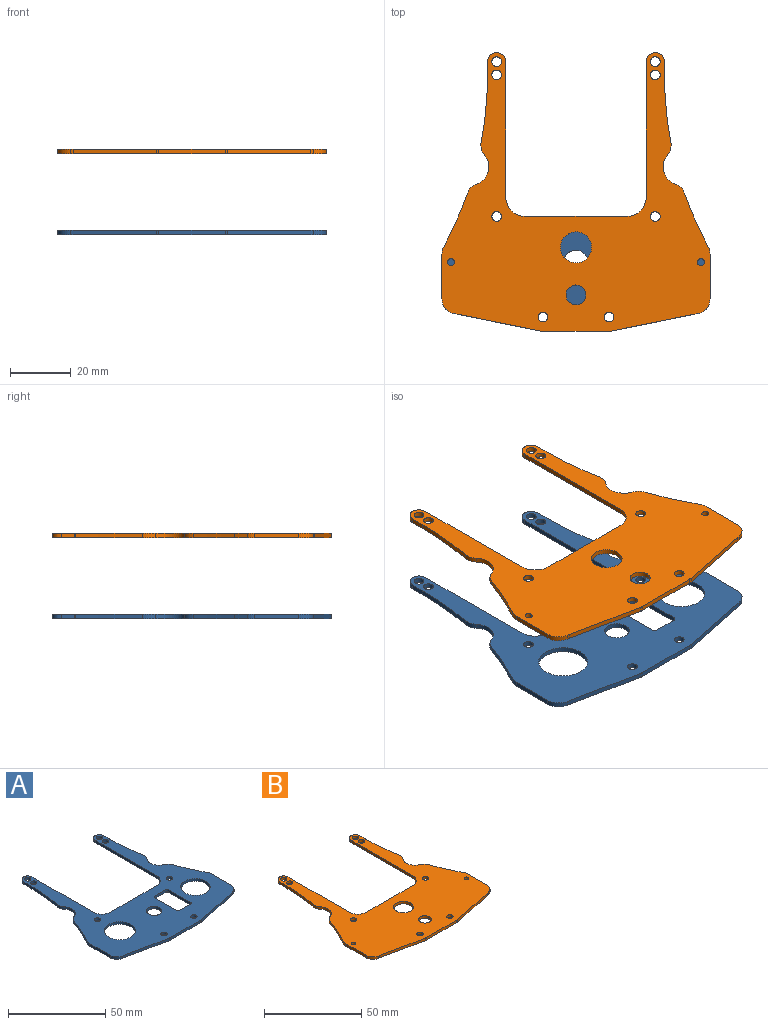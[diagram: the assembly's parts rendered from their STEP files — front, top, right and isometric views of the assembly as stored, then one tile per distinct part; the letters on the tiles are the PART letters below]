
ASSEMBLY  parts=2 mates=1
PART A: 58 faces, bbox 88x91.5x1.6 mm
  f0: cylinder r=116.85mm len=13.61mm, axis (0,0,-1), area 23.2mm2, adj f3,f4,f37,f50
  f1: cylinder r=116.85mm len=22mm, axis (0,0,-1), area 34.7mm2, adj f3,f4,f7,f38
  f2: cylinder r=116.85mm len=22mm, axis (0,0,-1), area 34.7mm2, adj f3,f4,f14,f35
  f3: plane 91.49x88mm, normal (0,0,1), area 3224.4mm2, adj f0,f1,f2,f5,f6,f7,f8,f9
  f4: plane 91.49x88mm, normal (0,0,-1), area 3224.4mm2, adj f0,f1,f2,f5,f6,f7,f8,f9
  f5: cylinder r=3mm len=6mm, axis (0,0,-1), area 14.8mm2, adj f3,f4,f6,f24
  f6: plane 4.35x1.57mm, normal (-1,0,0), area 6.8mm2, adj f3,f4,f5,f7
  f7: plane 1.57x0.09mm, normal (-1,0,0), area 0.1mm2, adj f1,f3,f4,f6
  f8: plane 28.21x5.75mm, normal (-0.2,-0.98,0), area 45.2mm2, adj f3,f4,f9,f53
  f9: cylinder r=4.68mm len=1.57mm, axis (0,0,-1), area 1.5mm2, adj f3,f4,f8,f10
  f10: plane 21.7x1.57mm, normal (0,-1,0), area 34.1mm2, adj f3,f4,f9,f11
  f11: cylinder r=4.68mm len=1.57mm, axis (0,0,-1), area 1.5mm2, adj f3,f4,f10,f12
  f12: plane 28.21x5.75mm, normal (0.2,-0.98,0), area 45.2mm2, adj f3,f4,f11,f54
  f13: cylinder r=116.85mm len=13.61mm, axis (0,0,-1), area 23.2mm2, adj f3,f4,f36,f57
  f14: plane 1.57x0.09mm, normal (1,0,0), area 0.1mm2, adj f2,f3,f4,f15
  f15: plane 4.35x1.57mm, normal (1,0,0), area 6.8mm2, adj f3,f4,f14,f16
  f16: cylinder r=3mm len=6mm, axis (0,0,-1), area 14.8mm2, adj f3,f4,f15,f17
  f17: plane 4.34x1.57mm, normal (-1,0,0), area 6.8mm2, adj f3,f4,f16,f18
  f18: plane 40.11x1.57mm, normal (-1,0,0), area 63mm2, adj f3,f4,f17,f19
  f19: cylinder r=6.35mm len=6.35mm, axis (0,0,-1), area 15.7mm2, adj f3,f4,f18,f20
  f20: plane 16.67x1.57mm, normal (0,1,0), area 26.2mm2, adj f3,f4,f19,f21
  f21: plane 16.67x1.57mm, normal (0,1,0), area 26.2mm2, adj f3,f4,f20,f22
  f22: cylinder r=6.35mm len=6.35mm, axis (0,0,-1), area 15.7mm2, adj f3,f4,f21,f23
  f23: plane 40.11x1.57mm, normal (1,0,0), area 63mm2, adj f3,f4,f22,f24
  f24: plane 4.34x1.57mm, normal (1,0,0), area 6.8mm2, adj f3,f4,f5,f23
  f25: cylinder r=1.6mm len=3.2mm, axis (0,0,-1), area 15.8mm2, adj f3,f4
  f26: cylinder r=1.6mm len=3.2mm, axis (0,0,-1), area 15.8mm2, adj f3,f4
  f27: cylinder r=1.6mm len=3.2mm, axis (0,0,-1), area 15.8mm2, adj f3,f4
  f28: cylinder r=1.6mm len=3.2mm, axis (0,0,-1), area 15.8mm2, adj f3,f4
  f29: cylinder r=1.6mm len=3.2mm, axis (0,0,-1), area 15.8mm2, adj f3,f4
  f30: cylinder r=1.6mm len=3.2mm, axis (0,0,-1), area 15.8mm2, adj f3,f4
  f31: cylinder r=1.6mm len=3.2mm, axis (0,0,-1), area 15.8mm2, adj f3,f4
  f32: cylinder r=1.6mm len=3.2mm, axis (0,0,-1), area 15.8mm2, adj f3,f4
  f33: cylinder r=6mm len=9.54mm, axis (0,0,1), area 18.2mm2, adj f3,f4,f37,f38
  f34: cylinder r=6mm len=9.54mm, axis (0,0,1), area 18.2mm2, adj f3,f4,f35,f36
  f35: cylinder r=5mm len=4.18mm, axis (0,0,-1), area 7mm2, adj f2,f3,f4,f34
  f36: cylinder r=5mm len=3.06mm, axis (0,0,1), area 7mm2, adj f3,f4,f13,f34
  f37: cylinder r=5mm len=3.06mm, axis (0,0,1), area 7mm2, adj f0,f3,f4,f33
  f38: cylinder r=5mm len=4.18mm, axis (0,0,-1), area 7mm2, adj f1,f3,f4,f33
  f39: cylinder r=7.5mm len=15mm, axis (0,0,1), area 74mm2, adj f3,f4
  f40: cylinder r=4mm len=8mm, axis (0,0,1), area 39.5mm2, adj f3,f4
  f41: plane 8x1.57mm, normal (0,-1,0), area 12.6mm2, adj f3,f4,f42,f48
  f42: cylinder r=1mm len=1.57mm, axis (0,0,1), area 2.5mm2, adj f3,f4,f41,f43
  f43: plane 16x1.57mm, normal (1,0,0), area 25.1mm2, adj f3,f4,f42,f44
  f44: cylinder r=1mm len=1.57mm, axis (0,0,1), area 2.5mm2, adj f3,f4,f43,f45
  f45: plane 8x1.57mm, normal (0,1,0), area 12.6mm2, adj f3,f4,f44,f46
  f46: cylinder r=1mm len=1.57mm, axis (0,0,1), area 2.5mm2, adj f3,f4,f45,f47
  f47: plane 16x1.57mm, normal (-1,0,0), area 25.1mm2, adj f3,f4,f46,f48
  f48: cylinder r=1mm len=1.57mm, axis (0,0,1), area 2.5mm2, adj f3,f4,f41,f47
  f49: cylinder r=8mm len=16mm, axis (0,0,1), area 78.9mm2, adj f3,f4
  f50: plane 4.09x2.05mm, normal (-0.89,0.45,0), area 7.2mm2, adj f0,f3,f4,f51
  f51: cylinder r=5mm len=2.24mm, axis (0,0,1), area 3.6mm2, adj f3,f4,f50,f52
  f52: plane 14.6x1.57mm, normal (-1,0,0), area 22.9mm2, adj f3,f4,f51,f53
  f53: cylinder r=5mm len=4.9mm, axis (0,0,1), area 10.8mm2, adj f3,f4,f8,f52
  f54: cylinder r=5mm len=4.9mm, axis (0,0,1), area 10.8mm2, adj f3,f4,f12,f55
  f55: plane 14.6x1.57mm, normal (1,0,0), area 22.9mm2, adj f3,f4,f54,f56
  f56: cylinder r=5mm len=2.24mm, axis (0,0,1), area 3.6mm2, adj f3,f4,f55,f57
  f57: plane 4.09x2.05mm, normal (0.89,0.45,0), area 7.2mm2, adj f3,f4,f13,f56
PART B: 55 faces, bbox 88x91.5x1.6 mm
  f0: cylinder r=3.18mm len=1.57mm, axis (0,0,-1), area 0mm2, adj f4,f5,f14,f47
  f1: cylinder r=116.85mm len=13.61mm, axis (0,0,-1), area 23.2mm2, adj f4,f5,f41,f43
  f2: cylinder r=116.85mm len=22mm, axis (0,0,-1), area 34.7mm2, adj f4,f5,f8,f42
  f3: cylinder r=116.85mm len=22mm, axis (0,0,-1), area 34.7mm2, adj f4,f5,f16,f39
  f4: plane 91.49x88mm, normal (0,0,1), area 3708.7mm2, adj f0,f1,f2,f3,f6,f7,f8,f9
  f5: plane 91.49x88mm, normal (0,0,-1), area 3708.7mm2, adj f0,f1,f2,f3,f6,f7,f8,f9
  f6: cylinder r=3mm len=6mm, axis (0,0,-1), area 14.8mm2, adj f4,f5,f7,f26
  f7: plane 4.35x1.57mm, normal (-1,0,0), area 6.8mm2, adj f4,f5,f6,f8
  f8: plane 1.57x0.09mm, normal (-1,0,0), area 0.1mm2, adj f2,f4,f5,f7
  f9: cylinder r=3.18mm len=1.57mm, axis (0,0,-1), area 0mm2, adj f4,f5,f10,f45
  f10: plane 27.26x5.56mm, normal (-0.2,-0.98,0), area 43.7mm2, adj f4,f5,f9,f11
  f11: cylinder r=4.68mm len=1.57mm, axis (0,0,-1), area 1.5mm2, adj f4,f5,f10,f12
  f12: plane 21.7x1.57mm, normal (0,-1,0), area 34.1mm2, adj f4,f5,f11,f13
  f13: cylinder r=4.68mm len=1.57mm, axis (0,0,-1), area 1.5mm2, adj f4,f5,f12,f14
  f14: plane 27.26x5.56mm, normal (0.2,-0.98,0), area 43.7mm2, adj f0,f4,f5,f13
  f15: cylinder r=116.85mm len=13.61mm, axis (0,0,-1), area 23.2mm2, adj f4,f5,f40,f46
  f16: plane 1.57x0.09mm, normal (1,0,0), area 0.1mm2, adj f3,f4,f5,f17
  f17: plane 4.35x1.57mm, normal (1,0,0), area 6.8mm2, adj f4,f5,f16,f18
  f18: cylinder r=3mm len=6mm, axis (0,0,-1), area 14.8mm2, adj f4,f5,f17,f19
  f19: plane 4.34x1.57mm, normal (-1,0,0), area 6.8mm2, adj f4,f5,f18,f20
  f20: plane 40.11x1.57mm, normal (-1,0,0), area 63mm2, adj f4,f5,f19,f21
  f21: cylinder r=6.35mm len=6.35mm, axis (0,0,-1), area 15.7mm2, adj f4,f5,f20,f22
  f22: plane 16.67x1.57mm, normal (0,1,0), area 26.2mm2, adj f4,f5,f21,f23
  f23: plane 16.67x1.57mm, normal (0,1,0), area 26.2mm2, adj f4,f5,f22,f24
  f24: cylinder r=6.35mm len=6.35mm, axis (0,0,-1), area 15.7mm2, adj f4,f5,f23,f25
  f25: plane 40.11x1.57mm, normal (1,0,0), area 63mm2, adj f4,f5,f24,f26
  f26: plane 4.34x1.57mm, normal (1,0,0), area 6.8mm2, adj f4,f5,f6,f25
  f27: cylinder r=1.6mm len=3.2mm, axis (0,0,-1), area 15.8mm2, adj f4,f5
  f28: cylinder r=1.6mm len=3.2mm, axis (0,0,-1), area 15.8mm2, adj f4,f5
  f29: cylinder r=1.6mm len=3.2mm, axis (0,0,-1), area 15.8mm2, adj f4,f5
  f30: cylinder r=1.6mm len=3.2mm, axis (0,0,-1), area 15.8mm2, adj f4,f5
  f31: cylinder r=1.6mm len=3.2mm, axis (0,0,-1), area 15.8mm2, adj f4,f5
  f32: cylinder r=1.6mm len=3.2mm, axis (0,0,-1), area 15.8mm2, adj f4,f5
  f33: cylinder r=1.6mm len=3.2mm, axis (0,0,-1), area 15.8mm2, adj f4,f5
  f34: cylinder r=1.6mm len=3.2mm, axis (0,0,-1), area 15.8mm2, adj f4,f5
  f35: cylinder r=3.26mm len=6.53mm, axis (0,0,-1), area 32.2mm2, adj f4,f5
  f36: cylinder r=5.08mm len=10.16mm, axis (0,0,-1), area 50.1mm2, adj f4,f5
  f37: cylinder r=6mm len=9.54mm, axis (0,0,1), area 18.2mm2, adj f4,f5,f41,f42
  f38: cylinder r=6mm len=9.54mm, axis (0,0,1), area 18.2mm2, adj f4,f5,f39,f40
  f39: cylinder r=5mm len=4.18mm, axis (0,0,-1), area 7mm2, adj f3,f4,f5,f38
  f40: cylinder r=5mm len=3.06mm, axis (0,0,1), area 7mm2, adj f4,f5,f15,f38
  f41: cylinder r=5mm len=3.06mm, axis (0,0,1), area 7mm2, adj f1,f4,f5,f37
  f42: cylinder r=5mm len=4.18mm, axis (0,0,-1), area 7mm2, adj f2,f4,f5,f37
  f43: plane 4.09x2.05mm, normal (-0.89,0.45,0), area 7.2mm2, adj f1,f4,f5,f53
  f44: plane 14.6x1.57mm, normal (-1,0,0), area 22.9mm2, adj f4,f5,f53,f54
  f45: plane 1.57x0.95mm, normal (-0.2,-0.98,0), area 1.5mm2, adj f4,f5,f9,f54
  f46: plane 4.09x2.05mm, normal (0.89,0.45,0), area 7.2mm2, adj f4,f5,f15,f52
  f47: plane 1.57x0.95mm, normal (0.2,-0.98,0), area 1.5mm2, adj f0,f4,f5,f51
  f48: plane 14.6x1.57mm, normal (1,0,0), area 22.9mm2, adj f4,f5,f51,f52
  f49: cylinder r=1.15mm len=2.3mm, axis (0,0,1), area 11.3mm2, adj f4,f5
  f50: cylinder r=1.15mm len=2.3mm, axis (0,0,1), area 11.3mm2, adj f4,f5
  f51: cylinder r=5mm len=4.9mm, axis (0,0,1), area 10.8mm2, adj f4,f5,f47,f48
  f52: cylinder r=5mm len=2.24mm, axis (0,0,-1), area 3.6mm2, adj f4,f5,f46,f48
  f53: cylinder r=5mm len=2.24mm, axis (0,0,-1), area 3.6mm2, adj f4,f5,f43,f44
  f54: cylinder r=5mm len=4.9mm, axis (0,0,1), area 10.8mm2, adj f4,f5,f44,f45
PLACE A t=(-41.31,-29.66,-1.57)mm fixed
PLACE B t=(-41.31,-29.66,25)mm
MATE fastened A.f30 <-> B.f32  axis (0,0,1) through (26.3,8.03,0)mm
